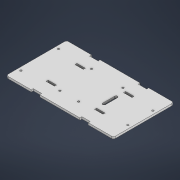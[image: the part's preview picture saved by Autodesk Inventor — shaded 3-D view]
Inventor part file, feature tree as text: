
AUTODESK INVENTOR PART (.ipt)
format: ipt  version: 2021 (Build 250183000, 183)  size: 198,144 bytes
history: native  units: mm
features: extrude x4, sketch x4, fillet x1
ambient origin geometry x8: Origin, YZ Plane, XZ Plane, XY Plane, X Axis, Y Axis, Z Axis, Center Point
bodies: Solid1 (feature_tree)
feature tree (9):
  extrude  "Extrusion1"  Depth=90.0mm
  extrude  "Extrusion2"  Depth=12.5mm
  fillet  "Fillet1"  Radius=3.005mm
  extrude  "Extrusion4"  TaperAngle=0.0deg  [1 undecoded]
  extrude  "Extrusion5"  Depth=3.0mm
  sketch  "Sketch1"  dims[d0=160.0mm d1=90.0mm]
  sketch  "Sketch2"  dims[d2=3.0mm d3=0.0mm d4=12.5mm d5=3.005mm]
  sketch  "Sketch4"  dims[d6=50.0mm d7=0.0mm d8=0.0mm]
  sketch  "Sketch5"  dims[d9=12.5mm d10=3.0mm d11=18.9mm d12=3.0mm d18=9.0mm d19=4.0mm d20=48.0mm d21=0.0mm d22=0.0mm d23=2.8mm d24=18.69mm d25=5.0mm d26=0.0mm d27=0.0mm d29=2.8mm d30=5.0mm d31=28.0mm d32=2.8mm d33=2.8mm d40=15.2mm d41=2.8mm d43=4.7mm d44=2.8mm d46=27.94mm d47=20.0mm d48=51.9mm d49=50.8mm d50=20.0mm d51=72.0mm]
note: 1 required parameter value undecoded (feature->parameter linkage not recoverable at this tier; creation-order binding heuristic only, values carry confidence <= 0.55)
